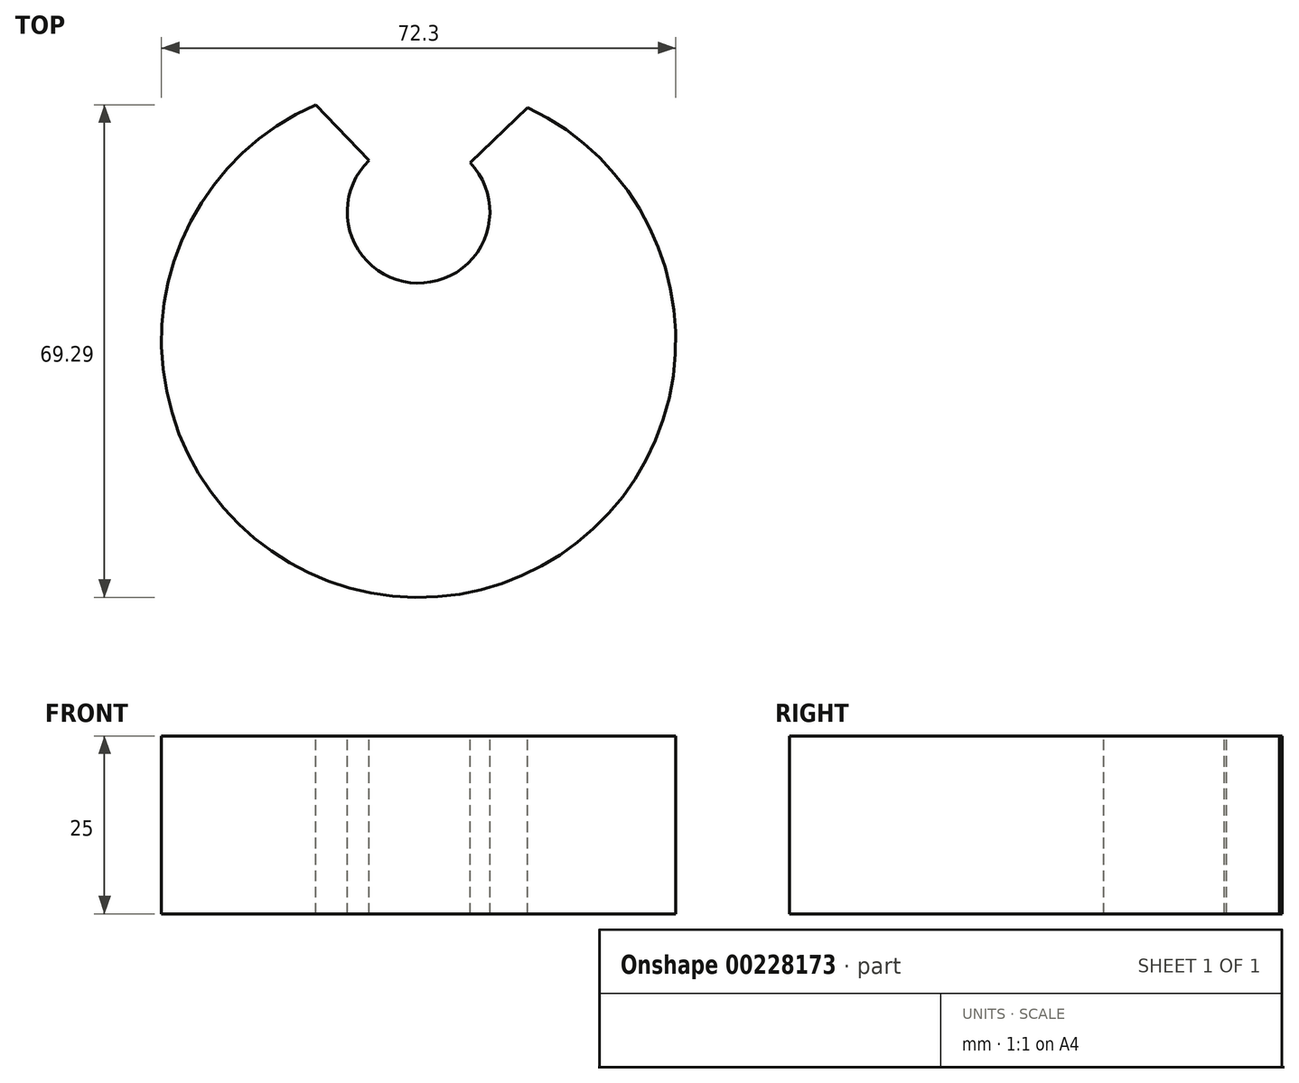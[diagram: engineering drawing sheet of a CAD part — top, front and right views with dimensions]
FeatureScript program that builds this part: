
annotation { "Feature Type Name" : "Feature", "Feature Type Description" : "" }
export const myFeature = defineFeature(function(context is Context, id is Id, definition is map)
    precondition{}
    {
        {
            var Q0;
            Q0=qCreatedBy(makeId("Top.planeOp"),FACE);
            var sketch = newSketch(context, id + "F0", { "sketchPlane" : qUnion([Q0])});
            skCircle(sketch, "E0", {"center": v(0, 0) * mm, "radius": 36.15 * mm});
            skSolve(sketch);
        }
        {
            var Q0;
            Q0=makeQuery(id+"F0.imprint","IMPRINT",FACE,{"disambiguationData":[TD([[makeQuery(id+"F0.imprint","IMPRINT",EDGE,{"derivedFrom":sQuery(id+"F0.wireOp",EDGE,"E0")}),1.0]])]});
            extrude(context, id + "F1", {"entities" : qUnion([Q0]), "depth" : 25 * mm});
        }
        {
            var Q0;
            Q0=makeQuery(id+"F1.opExtrude","CAP_FACE",FACE,{"disambiguationData":[OSD([sQuery(id+"F0.wireOp",EDGE,"E0")])],"isStart":false});
            var sketch = newSketch(context, id + "F2", { "sketchPlane" : qUnion([Q0])});
            skLineSegment(sketch, "E1", {"start": v(0, 0) * mm, "end": v(0, 36.15) * mm});
            skCircle(sketch, "E2", {"center": v(0, 18.08) * mm, "radius": 10.03 * mm});
            skLineSegment(sketch, "E3", {"start": v(0, 18.08) * mm, "end": v(-14.43, 33.14) * mm});
            skLineSegment(sketch, "E4", {"start": v(0, 18.08) * mm, "end": v(15.32, 32.74) * mm});
            skSolve(sketch);
        }
        {
            var Q0;
            {var subQ0=sQuery(id+"F2.wireOp",EDGE,"E1");var subQ1=makeQuery(id+"F1.opExtrude","CAP_EDGE",EDGE,{"disambiguationData":[OSD([sQuery(id+"F0.wireOp",EDGE,"E0")])],"isStart":false});var subQ2=makeQuery(id+"F2.imprint","INTERSECT",VERTEX,{"derivedFrom":[subQ1,subQ0]});Q0=makeQuery(id+"F2.imprint","IMPRINT",FACE,{"disambiguationData":[TD([[makeQuery(id+"F2.imprint","IMPRINT",EDGE,{"disambiguationData":[TD([[subQ2,1.0]])],"derivedFrom":subQ0}),1.0]])]});}
            var Q1;
            {var subQ0=sQuery(id+"F2.wireOp",EDGE,"E1");var subQ1=makeQuery(id+"F1.opExtrude","CAP_EDGE",EDGE,{"disambiguationData":[OSD([sQuery(id+"F0.wireOp",EDGE,"E0")])],"isStart":false});var subQ2=makeQuery(id+"F2.imprint","INTERSECT",VERTEX,{"derivedFrom":[subQ1,subQ0]});Q1=makeQuery(id+"F2.imprint","IMPRINT",FACE,{"disambiguationData":[TD([[makeQuery(id+"F2.imprint","IMPRINT",EDGE,{"disambiguationData":[TD([[subQ2,1.0]])],"derivedFrom":subQ0}),-1.0]])]});}
            var Q2;
            {var subQ1=sQuery(id+"F2.wireOp",EDGE,"E1");var subQ3=sQuery(id+"F2.wireOp",EDGE,"E2");var subQ4=makeQuery(id+"F2.imprint","INTERSECT",VERTEX,{"disambiguationData":[OD(1.0)],"derivedFrom":[subQ1,subQ3]});Q2=makeQuery(id+"F2.imprint","IMPRINT",FACE,{"disambiguationData":[TD([[makeQuery(id+"F2.imprint","IMPRINT",EDGE,{"disambiguationData":[TD([[subQ4,1.0]])],"derivedFrom":subQ3}),1.0]])]});}
            var Q3;
            {var subQ1=sQuery(id+"F2.wireOp",EDGE,"E1");var subQ3=sQuery(id+"F2.wireOp",EDGE,"E2");var subQ4=makeQuery(id+"F2.imprint","INTERSECT",VERTEX,{"disambiguationData":[OD(1.0)],"derivedFrom":[subQ1,subQ3]});Q3=makeQuery(id+"F2.imprint","IMPRINT",FACE,{"disambiguationData":[TD([[makeQuery(id+"F2.imprint","IMPRINT",EDGE,{"disambiguationData":[TD([[subQ4,-1.0]])],"derivedFrom":subQ3}),1.0]])]});}
            var Q4;
            {var subQ1=sQuery(id+"F2.wireOp",EDGE,"E1");var subQ3=sQuery(id+"F2.wireOp",EDGE,"E2");var subQ4=makeQuery(id+"F2.imprint","INTERSECT",VERTEX,{"disambiguationData":[OD(0.0)],"derivedFrom":[subQ1,subQ3]});Q4=makeQuery(id+"F2.imprint","IMPRINT",FACE,{"disambiguationData":[TD([[makeQuery(id+"F2.imprint","IMPRINT",EDGE,{"disambiguationData":[TD([[subQ4,1.0]])],"derivedFrom":subQ3}),1.0]])]});}
            var Q5;
            {var subQ1=sQuery(id+"F2.wireOp",EDGE,"E1");var subQ3=sQuery(id+"F2.wireOp",EDGE,"E2");var subQ4=makeQuery(id+"F2.imprint","INTERSECT",VERTEX,{"disambiguationData":[OD(0.0)],"derivedFrom":[subQ1,subQ3]});Q5=makeQuery(id+"F2.imprint","IMPRINT",FACE,{"disambiguationData":[TD([[makeQuery(id+"F2.imprint","IMPRINT",EDGE,{"disambiguationData":[TD([[subQ4,-1.0]])],"derivedFrom":subQ3}),1.0]])]});}
            extrude(context, id + "F3", {"entities" : qUnion([Q0, Q1, Q2, Q3, Q4, Q5]), "operationType" : NewBodyOperationType.REMOVE, "oppositeDirection" : true, "depth" : 25 * mm});
        }
    });
